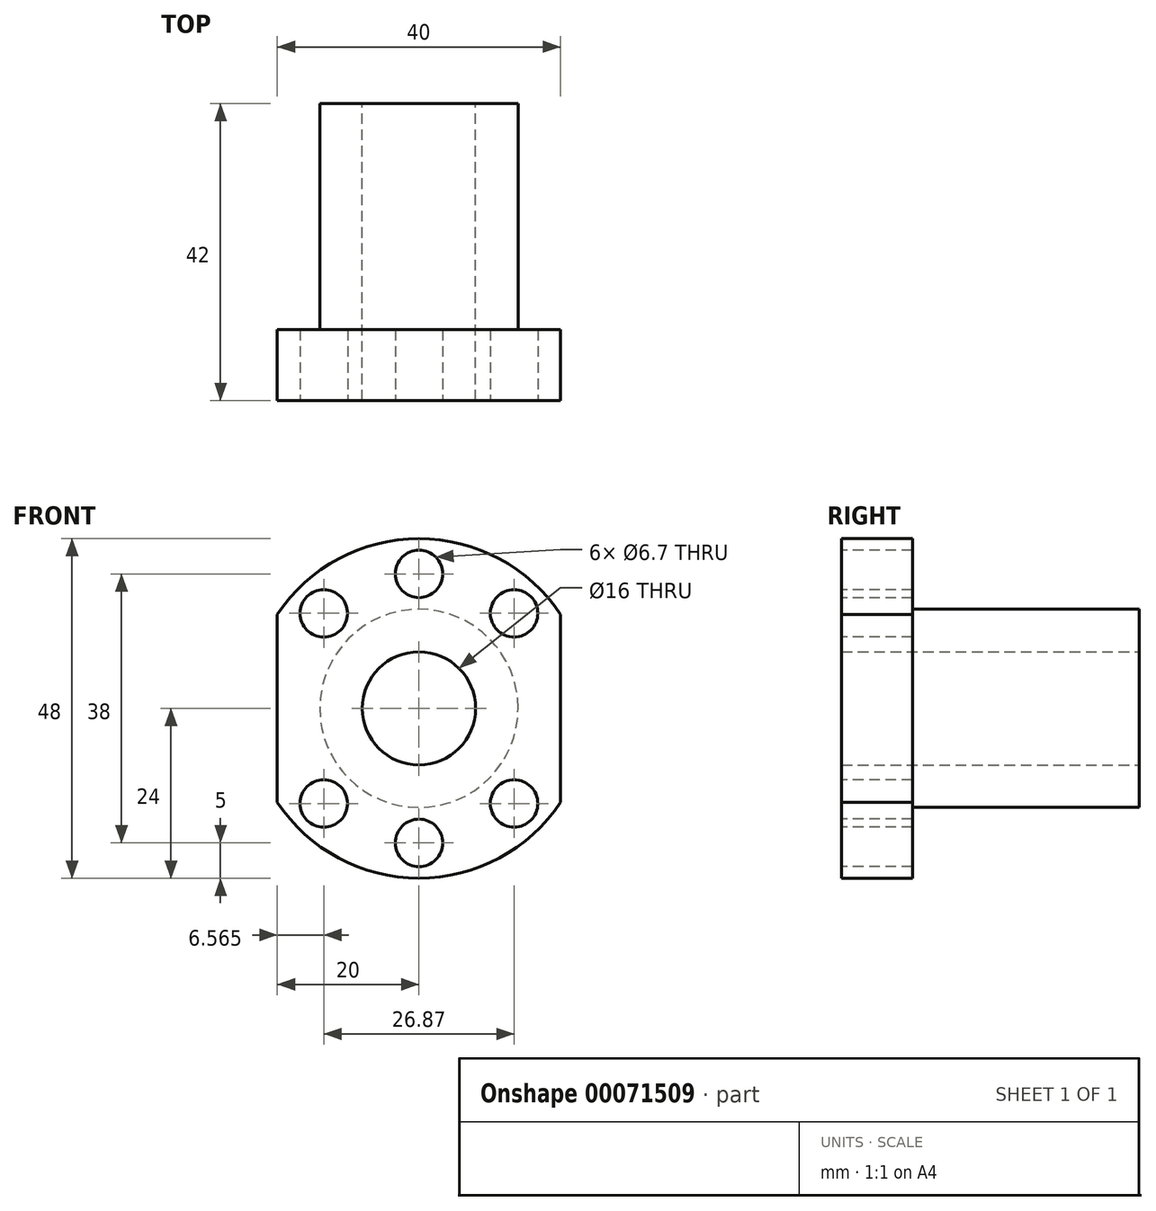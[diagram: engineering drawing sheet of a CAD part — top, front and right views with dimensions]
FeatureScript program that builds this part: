
annotation { "Feature Type Name" : "Feature", "Feature Type Description" : "" }
export const myFeature = defineFeature(function(context is Context, id is Id, definition is map)
    precondition{}
    {
        {
            var Q0;
            Q0=qCreatedBy(makeId("Front.planeOp"),FACE);
            var sketch = newSketch(context, id + "F0", { "sketchPlane" : qUnion([Q0])});
            skCircle(sketch, "E0", {"center": v(0, 0) * mm, "radius": 14 * mm});
            skCircle(sketch, "E1", {"center": v(0, 0) * mm, "radius": 8 * mm});
            skSolve(sketch);
        }
        {
            var Q0;
            Q0=makeQuery(id+"F0.imprint","IMPRINT",FACE,{"disambiguationData":[TD([[makeQuery(id+"F0.imprint","IMPRINT",EDGE,{"derivedFrom":sQuery(id+"F0.wireOp",EDGE,"E0")}),1.0]])]});
            extrude(context, id + "F1", {"entities" : qUnion([Q0]), "depth" : 42 * mm});
        }
        {
            var Q0;
            Q0=makeQuery(id+"F1.opExtrude","CAP_FACE",FACE,{"disambiguationData":[OSD([sQuery(id+"F0.wireOp",EDGE,"E0"),sQuery(id+"F0.wireOp",EDGE,"E1")])],"isStart":false});
            var sketch = newSketch(context, id + "F2", { "sketchPlane" : qUnion([Q0])});
            skArc(sketch, "E2", {"start": v(-20, -13.27) * mm, "mid": v(0, -24) * mm, "end": v(20, -13.27) * mm});
            skLineSegment(sketch, "E3.left", {"start": v(-20, 13.27) * mm, "end": v(-20, -13.27) * mm});
            skLineSegment(sketch, "E3.right", {"start": v(20, 13.27) * mm, "end": v(20, -13.27) * mm});
            skArc(sketch, "E4.trimOffspring", {"start": v(20, 13.27) * mm, "mid": v(0, 24) * mm, "end": v(-20, 13.27) * mm});
            skCircle(sketch, "E5", {"center": v(0, 19) * mm, "radius": 3.35 * mm});
            skCircle(sketch, "E6.1.0", {"center": v(-13.44, 13.44) * mm, "radius": 3.35 * mm});
            skCircle(sketch, "E6.3.0", {"center": v(-13.44, -13.44) * mm, "radius": 3.35 * mm});
            skCircle(sketch, "E6.4.0", {"center": v(0, -19) * mm, "radius": 3.35 * mm});
            skCircle(sketch, "E6.5.0", {"center": v(13.44, -13.44) * mm, "radius": 3.35 * mm});
            skCircle(sketch, "E6.7.0", {"center": v(13.44, 13.44) * mm, "radius": 3.35 * mm});
            skCircle(sketch, "E7", {"center": v(0, 0) * mm, "radius": 8 * mm});
            skSolve(sketch);
        }
        {
            var Q0;
            Q0=makeQuery(id+"F2.imprint","IMPRINT",FACE,{"disambiguationData":[TD([[makeQuery(id+"F2.imprint","IMPRINT",EDGE,{"derivedFrom":makeQuery(id+"F1.opExtrude","CAP_EDGE",EDGE,{"disambiguationData":[OSD([sQuery(id+"F0.wireOp",EDGE,"E0")])],"isStart":false})}),1.0]])]});
            var Q1;
            Q1=makeQuery(id+"F2.imprint","IMPRINT",FACE,{"disambiguationData":[TD([[makeQuery(id+"F2.imprint","IMPRINT",EDGE,{"derivedFrom":sQuery(id+"F2.wireOp",EDGE,"E2")}),1.0]])]});
            extrude(context, id + "F3", {"entities" : qUnion([Q0, Q1]), "operationType" : NewBodyOperationType.ADD, "oppositeDirection" : true, "depth" : 10 * mm});
        }
    });
